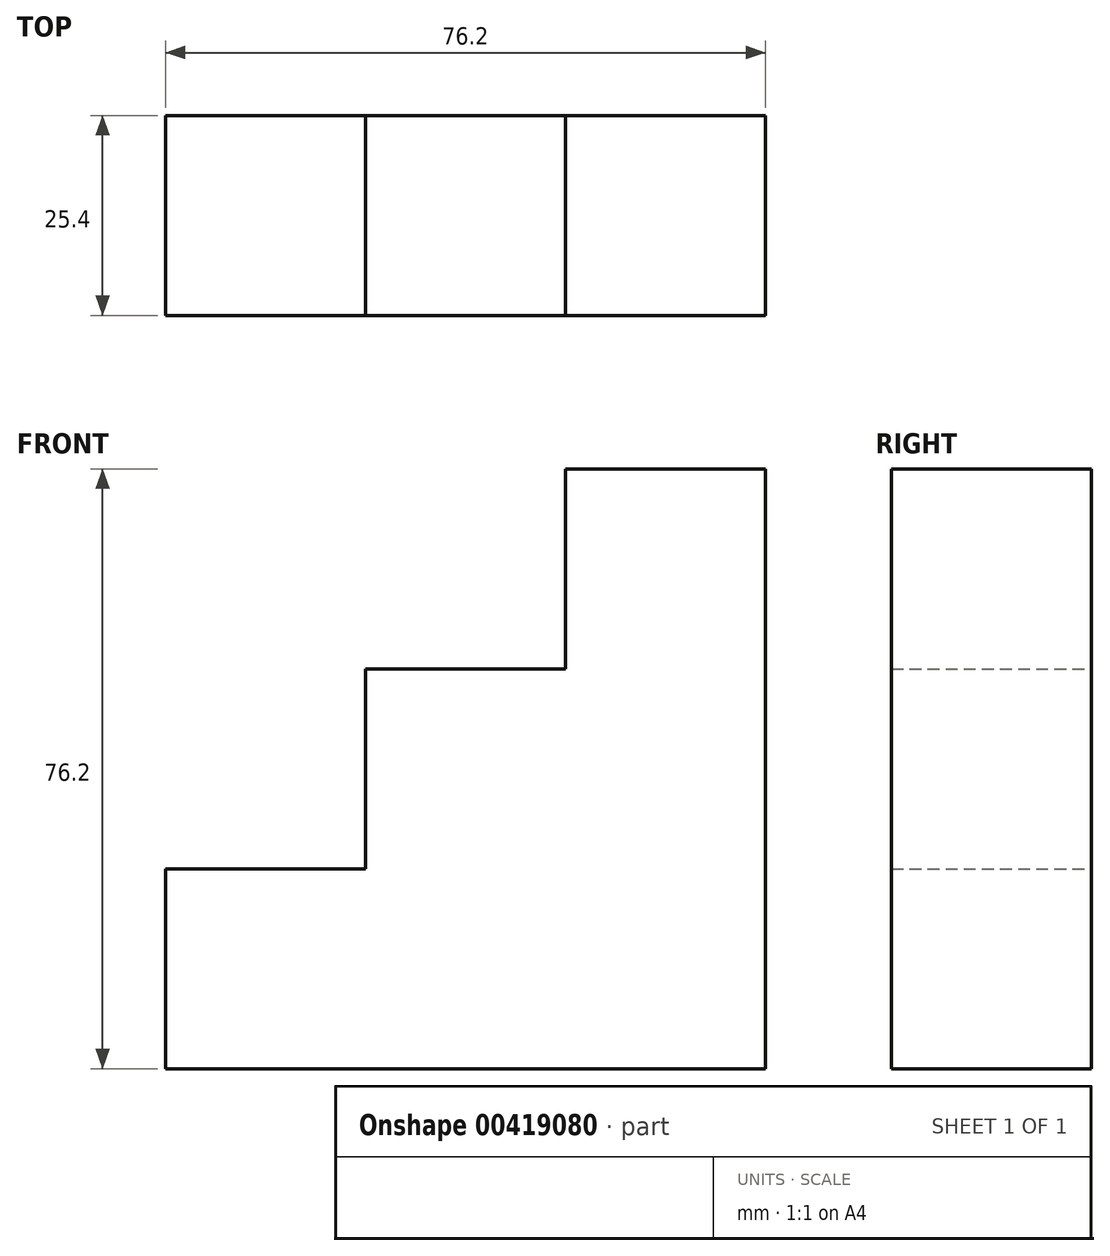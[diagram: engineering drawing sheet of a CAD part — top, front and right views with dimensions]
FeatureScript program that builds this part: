
annotation { "Feature Type Name" : "Feature", "Feature Type Description" : "" }
export const myFeature = defineFeature(function(context is Context, id is Id, definition is map)
    precondition{}
    {
        {
            var Q0;
            Q0=qCreatedBy(makeId("Front.planeOp"),FACE);
            var sketch = newSketch(context, id + "F0", { "sketchPlane" : qUnion([Q0])});
            skLineSegment(sketch, "E0", {"start": v(0, 0) * mm, "end": v(-76.2, 0) * mm});
            skLineSegment(sketch, "E1", {"start": v(-76.2, 0) * mm, "end": v(-76.2, 25.4) * mm});
            skLineSegment(sketch, "E2", {"start": v(-76.2, 25.4) * mm, "end": v(-50.8, 25.4) * mm});
            skLineSegment(sketch, "E3", {"start": v(-50.8, 25.4) * mm, "end": v(-50.8, 50.8) * mm});
            skLineSegment(sketch, "E4", {"start": v(-50.8, 50.8) * mm, "end": v(-25.4, 50.8) * mm});
            skLineSegment(sketch, "E5", {"start": v(-25.4, 50.8) * mm, "end": v(-25.4, 76.2) * mm});
            skLineSegment(sketch, "E6", {"start": v(-25.4, 76.2) * mm, "end": v(0, 76.2) * mm});
            skLineSegment(sketch, "E7", {"start": v(0, 76.2) * mm, "end": v(0, 0) * mm});
            skSolve(sketch);
        }
        {
            var Q0;
            Q0=makeQuery(id+"F0.imprint","IMPRINT",FACE,{"disambiguationData":[TD([[makeQuery(id+"F0.imprint","IMPRINT",EDGE,{"derivedFrom":sQuery(id+"F0.wireOp",EDGE,"E0")}),-1.0]])]});
            extrude(context, id + "F1", {"entities" : qUnion([Q0]), "depth" : 25.4 * mm});
        }
    });
